# Revit family: RN 86132 Optiflex-Valvola diritta
name_source: partatom
category: Rohrzubehör
units: mm (PartAtom-declared; Revit-internal decimal feet)

## family parameters
Arbeitsebenenbasiert = Nein
Beim Laden mit Abzugskörper schneiden = Nein
Bemaßung runder Anschluss = Durchmesser verwenden
Gemeinsam genutzt = Nein
Immer vertikal = Ja
Teiletyp = Ventil - Zerlegung in

## types (1)
- DN 20
    1.010.00.2 Blattnummer der Richtlinie = 17
    1.010.00.3 Ausgabedatum (Monat) der Richtlinie = 201601
    1.010.00.4 Herstellername = R. Nussbaum AG
    1.010.00.5 Revisionsdatum der Datei = 20190528
    1.010.00.6 Webadresse des Herstellers = http://www.nussbaum.ch
    1.100.00.3 Sortiernummer für Anzeigereihenfolge = 1
    1.100.00.4 Produktbezeichnung = Absperrarmaturen
    1.800.00.3 TGA-Nummer = 00108600000000000000000000000200700000000000000001???00000
    1.810.00.3 Hersteller-Bestellnummer = 86132.21
    1.810.00.4 DATANORM-Nummer = 86132.21
    1.810.00.5 StLB-Nummer = 381.414
    1.810.00.6 GTIN-Nummer = 7612945733061
    1.960/3L.00.8 Link (URL) = https://www.nussbaum.ch
    17.700.00.30 Produktbeschreibung = 86132.21, Optiflex-Geradsitzventil, mit Wandflansch, DN=20
    17.700.00.4 Armaturentyp = 1
    17.700.00.5 Nennweite DN = 20
    17.700.00.6 kvs-Wert [m3/h] = 5.6
    17.700.00.7 Maximale Betriebstemperatur TB [°C] = 70
    17.700.00.8 Maximaler Betriebsdruck (Arbeitsdruck) ps [1.0 · 105 Pa] = 10
    CONNECTOR0_DIAMETER_dX_0r = 20 mm
    CONNECTOR0_dX_00 = 33 mm  [stored 0.108268 ft]
    CONNECTOR0_dX_01 = 18 mm
    CONNECTOR0_ref_dX = 33 mm  [stored 0.108268 ft]
    CONNECTOR1_DIAMETER_dX_0r = 20 mm
    CONNECTOR1_dX_00 = 18 mm
    CONNECTOR1_dX_01 = 33 mm  [stored 0.108268 ft]
    CONNECTOR1_ref_dX = 33 mm  [stored 0.108268 ft]
    Connector Visibility = Nein
    EnclosingSpace Visibility = Nein
    Hersteller = R. Nussbaum AG
    Modell = 86132.21
    R. Nussbaum AG 86132.21 de Visibility = Ja
    Typenkommentare = Optiflex-Valvola diritta  DN 20
    URL = https://www.nussbaum.ch

note: [stored X ft] marks values corroborated as IEEE doubles in the binary element streams (Revit-internal decimal feet)

## geometry (parser evidence)
native form markers: Sweep x3
no freeform markers — native parametric forms only
